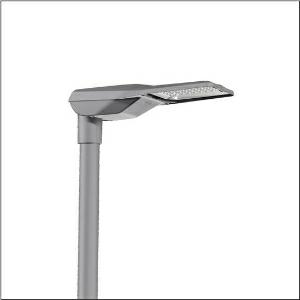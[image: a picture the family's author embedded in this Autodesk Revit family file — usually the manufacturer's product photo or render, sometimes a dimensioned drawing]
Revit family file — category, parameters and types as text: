
# Revit family: streetlight_sl_21_mini___st1_0a_5xe6d43a08gb_1c7e
name_source: partatom
category: Lighting Fixtures
units: mm (PartAtom-declared; Revit-internal decimal feet)

## family parameters
Cut with Voids When Loaded = No
Host = Face
Light Source = No
Part Type = Normal
Room Calculation Point = No
Round Connector Dimension = Use Diameter
Shared = No

## types (1)
- --- (1 x LED, 6180 lm, 40.4 W, 4000K)
    Apparent Load = 40 VA
    CIE Flux Codes = 37 72 97 100 100
    Color Rendering = 70
    Color Temperature = 4000K
    Default Elevation = 1800 mm
    Description = Streetlight SL 21 mini, mast luminaire, primary light control with lens, of PMMA, primary optical cover: cover, of toughened safety glass, transparent, light distribution: ST1.0a, light emission: direct distribution, primary light characteristic: asymmetric, installation type: post-top, side-entry, LED, 3G 1.5mm², High Power LED, rated luminous flux: 6.180lm, luminous efficacy: 153lm/W, light colour: 740, colour temperature: 4000K, control gear: Easy, control: overheat protection, constant luminous flux control, time-dependent luminous flux control, flexible luminous flux parameterisation, mains connection: 230..240V, AC, 50/60Hz, connection cable pre-assembled, cable length: 6,5m, wiring characteristics: H07RN-F, start of lifetime: 40W, end of service life: 41W, reduction: 19W, luminaire housing, of diecast aluminium, powder-coated, Siteco® metallic grey (DB 702S), corrosivity category C5 mid according to DIN EN ISO 12944, please order mast flange separately, inclination adjustable: 0°, 5°, 10°, 15°, sealing non-destructively replaceable, multi-level sealing system, length: 628mm, width: 235mm, height: 110mm, mast flange for spigot size: 42mm (side-entry): 5XC10008XM4, 60/48mm (side-entry/post-top): 5XC10108XM2, 76/60mm (side-entry/post-top): 5XC10108XM1, mounting height: 4..8m, protection rating (complete): IP66, insulation class (complete): insulation class II (safety insulation), certification: CE, ENEC, ENEC+, VDE, impact resistance: IK10, permissible operating ambient temperature for outdoor applications: -40..+50°C, standard-compliant lighting for roads and squares, packaging unit: 1 piece

Light Distribution: ST1.0a
    Height = 110 mm
    Lamp = 1 x LED
    Lamp Light Flux = 6180 lm
    Lamp Power = 40.4 W
    Lamp count = 1
    Length = 625 mm
    Luminous efficacy = 153 lm/W
    Manufacturer = Siteco
    ModVariant = No
    Model = 5XE6D43A08GB
    Number of Poles = 1
    OnlyDefault = Yes
    Power Factor = 1
    Product Name = Streetlight SL 21 mini | ST1.0a
    Product group = mast luminaire | pylon top
    ProductGroupID = 6100
    Protection Class = Protection class II
    Protection Degree = IP 66
    RLX_Detail_Level = 1
    RLX_Emergency_Light_Flux = 0 lm
    RLX_Emergency_Type = 0
    RLX_Emergency_Type_DB = No
    RlxData = <blob elided: 25889 chars, md5=8c788846>
    Socket = socket
    Standby Power = 0 W
    System Light Flux = 6180 lm
    System Power = 40 W
    Type Comments = factory setting: luminous flux: 100 % | Output Level: 100 % | 812 mA
    Type Image = l_1003519.jpg
    URL = http://relux.com
    VarID = @adj_209627
    Voltage = 0 V
    Weight = 0.00 kg
    Width = 234 mm

## geometry (parser evidence)
native form markers: Blend x4, Sweep x12
no freeform markers — native parametric forms only
